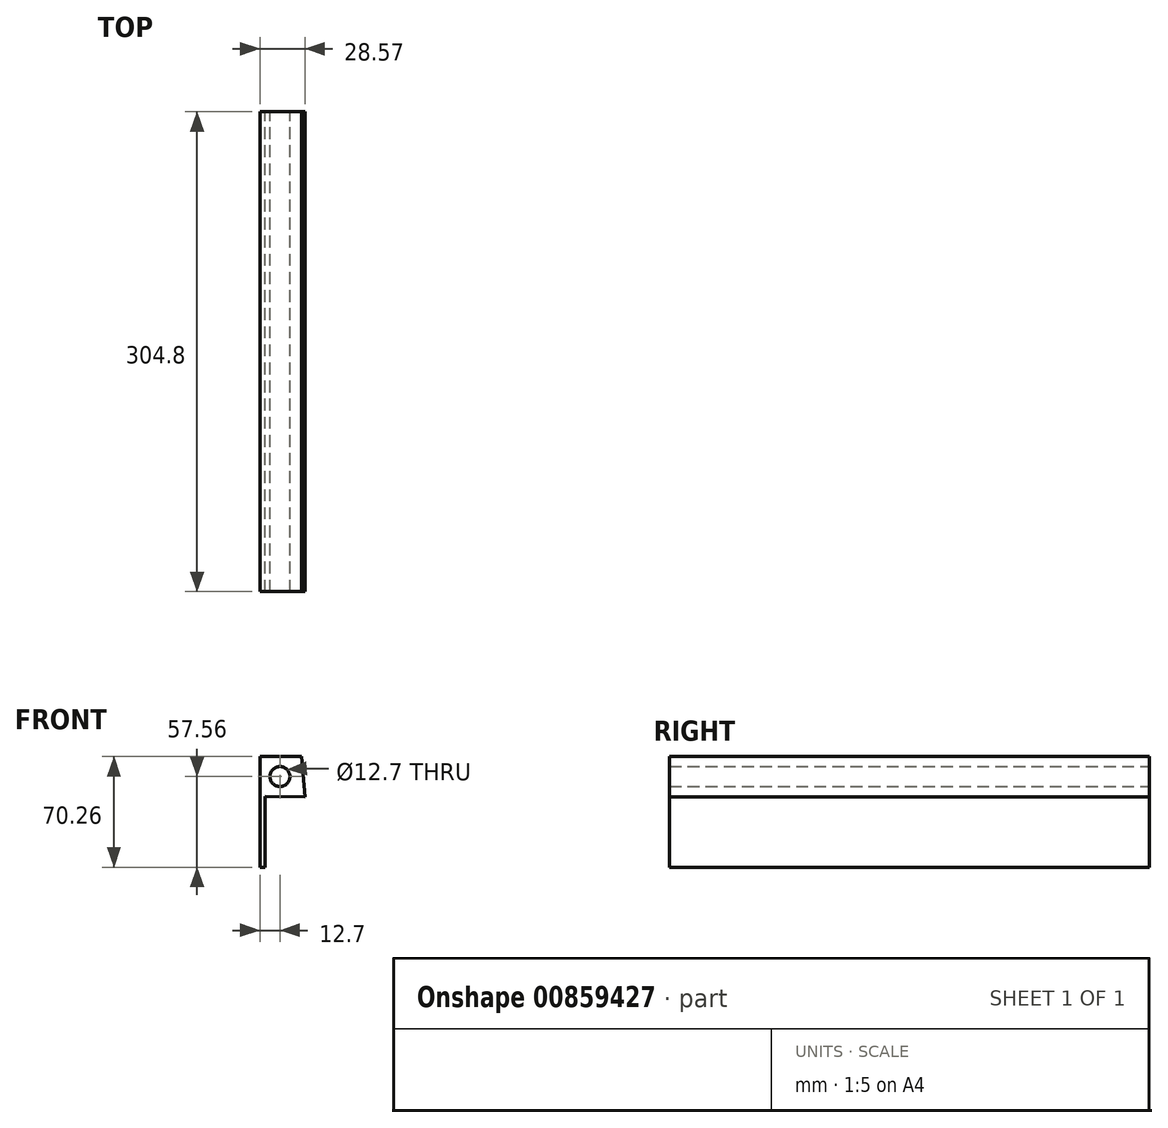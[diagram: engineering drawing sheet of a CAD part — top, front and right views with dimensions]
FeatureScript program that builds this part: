
annotation { "Feature Type Name" : "Feature", "Feature Type Description" : "" }
export const myFeature = defineFeature(function(context is Context, id is Id, definition is map)
    precondition{}
    {
        {
            var Q0;
            Q0=qCreatedBy(makeId("Front.planeOp"),FACE);
            var sketch = newSketch(context, id + "F0", { "sketchPlane" : qUnion([Q0])});
            skLineSegment(sketch, "E0.top", {"start": v(13.75, 12.7) * mm, "end": v(-12.7, 12.7) * mm});
            skLineSegment(sketch, "E0.left", {"start": v(15.87, -12.82) * mm, "end": v(13.75, 12.7) * mm});
            skLineSegment(sketch, "E0.right", {"start": v(-12.7, -12.7) * mm, "end": v(-12.7, 12.7) * mm});
            skPoint(sketch, "E0.middle", {"position": v(0, 0) * mm});
            skLineSegment(sketch, "E1", {"start": v(-12.7, -12.7) * mm, "end": v(15.87, -12.82) * mm});
            skLineSegment(sketch, "E2.bottom", {"start": v(-12.7, -12.7) * mm, "end": v(-9.52, -12.7) * mm});
            skLineSegment(sketch, "E2.top", {"start": v(-12.7, -57.56) * mm, "end": v(-9.52, -57.56) * mm});
            skLineSegment(sketch, "E2.left", {"start": v(-12.7, -12.7) * mm, "end": v(-12.7, -57.56) * mm});
            skLineSegment(sketch, "E2.right", {"start": v(-9.53, -12.7) * mm, "end": v(-9.52, -57.56) * mm});
            skCircle(sketch, "E3", {"center": v(0, 0) * mm, "radius": 6.35 * mm});
            skSolve(sketch);
        }
        {
            var Q0;
            {var subQ4=sQuery(id+"F0.wireOp",EDGE,"E2.top");Q0=makeQuery(id+"F0.imprint","IMPRINT",FACE,{"disambiguationData":[TD([[makeQuery(id+"F0.imprint","IMPRINT",EDGE,{"derivedFrom":subQ4}),1.0]])]});}
            var Q1;
            Q1=makeQuery(id+"F0.imprint","IMPRINT",FACE,{"disambiguationData":[TD([[makeQuery(id+"F0.imprint","IMPRINT",EDGE,{"derivedFrom":sQuery(id+"F0.wireOp",EDGE,"4bG2bUtd-Br3L-ptL1-f64M-MAjjOEqcTu0n")}),1.0]])]});
            var Q2;
            Q2=makeQuery(id+"F0.imprint","IMPRINT",FACE,{"disambiguationData":[TD([[makeQuery(id+"F0.imprint","IMPRINT",EDGE,{"derivedFrom":sQuery(id+"F0.wireOp",EDGE,"E0.top")}),1.0]])]});
            var Q3;
            {var subQ0=sQuery(id+"F0.wireOp",EDGE,"E2.bottom");Q3=makeQuery(id+"F0.imprint","IMPRINT",FACE,{"disambiguationData":[TD([[makeQuery(id+"F0.imprint","IMPRINT",EDGE,{"derivedFrom":subQ0}),-1.0]])]});}
            extrude(context, id + "F1", {"entities" : qUnion([Q0, Q1, Q2, Q3]), "depth" : 304.8 * mm, "offsetDistance" : 25.4 * mm});
        }
    });
